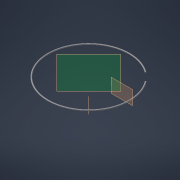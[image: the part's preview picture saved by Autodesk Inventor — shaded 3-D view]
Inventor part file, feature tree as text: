
AUTODESK INVENTOR PART (.ipt)
format: ipt  version: 2021 (Build 250183000, 183)  size: 125,440 bytes
history: native  units: mm
features: other x8, sketch x2, revolve x1, extrude x1, reference x1
ambient origin geometry x8: Origin, YZ Plane, XZ Plane, XY Plane, X Axis, Y Axis, Z Axis, Center Point
bodies: Body1 (feature_tree)
feature tree (13):
  other  "Твердое тело1"
  other  "РабПлоскость1"
  sketch  "Эскиз1"
  other  "РабОсь1"
  revolve  "Вращение1"
  other  "РабПлоскость2"
  extrude  "Выдавливание1"  Depth=0.1mm
  reference  "Ссылка1"
  sketch  "Эскиз2"
  other  "<userpath>\Documents\GitHub\Tesla_coil_V1\3dModels\TeslaCoil.iam"
  other  "TeslaCoil.iam"
  other  "RackeSecondary:2"
  other  "Cap:1"
